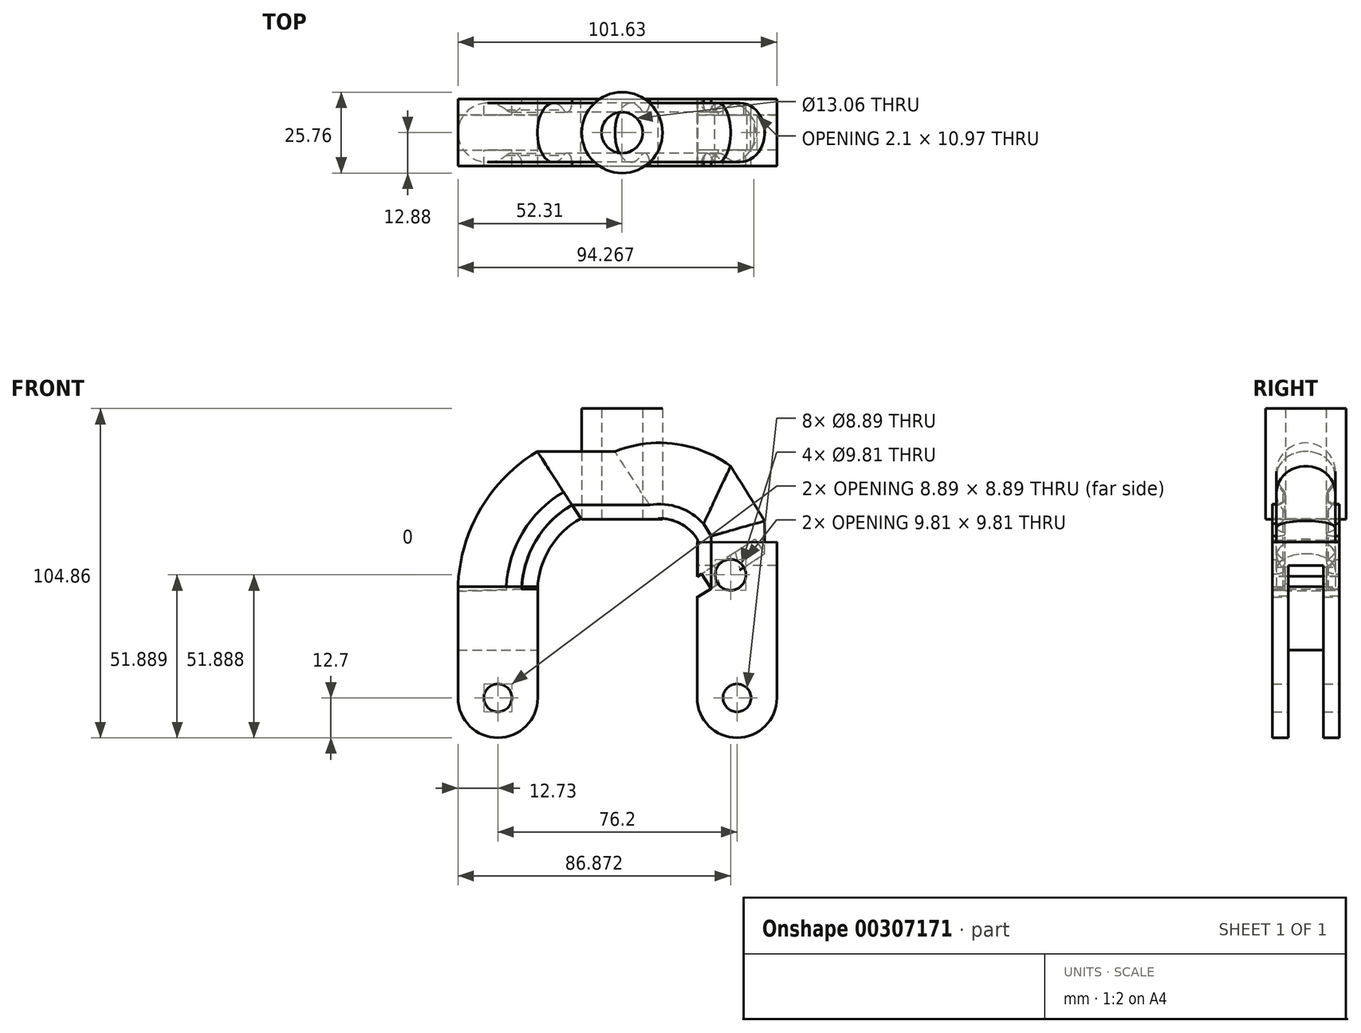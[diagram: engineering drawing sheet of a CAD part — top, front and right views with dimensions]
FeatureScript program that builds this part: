
annotation { "Feature Type Name" : "Feature", "Feature Type Description" : "" }
export const myFeature = defineFeature(function(context is Context, id is Id, definition is map)
    precondition{}
    {
        {
            var Q0;
            Q0=qCreatedBy(makeId("Front.planeOp"),FACE);
            var sketch = newSketch(context, id + "F0", { "sketchPlane" : qUnion([Q0])});
            skCircle(sketch, "E0", {"center": v(-39.58, 0) * mm, "radius": 12.7 * mm});
            skCircle(sketch, "E1", {"center": v(36.62, 0) * mm, "radius": 12.7 * mm});
            skLineSegment(sketch, "E2", {"start": v(-39.58, 0) * mm, "end": v(36.62, 0) * mm, "construction": true});
            skLineSegment(sketch, "E3", {"start": v(23.92, 0) * mm, "end": v(23.92, 49.53) * mm});
            skLineSegment(sketch, "E4", {"start": v(49.32, 0) * mm, "end": v(49.32, 49.66) * mm});
            skCircle(sketch, "E5", {"center": v(34.56, 39.19) * mm, "radius": 4.9 * mm});
            skCircle(sketch, "E6", {"center": v(-39.58, 0) * mm, "radius": 4.45 * mm});
            skCircle(sketch, "E7", {"center": v(36.62, 0) * mm, "radius": 4.45 * mm});
            skLineSegment(sketch, "E8", {"start": v(-26.88, 0) * mm, "end": v(-26.88, 48.71) * mm});
            skLineSegment(sketch, "E9", {"start": v(-26.88, 48.71) * mm, "end": v(-26.88, 0) * mm});
            skLineSegment(sketch, "E10", {"start": v(-52.28, 0) * mm, "end": v(-52.28, 35.38) * mm});
            skLineSegment(sketch, "E11", {"start": v(-52.28, 35.38) * mm, "end": v(-26.88, 35.38) * mm});
            skLineSegment(sketch, "E12", {"start": v(0, 0) * mm, "end": v(0, 75.66) * mm, "construction": true});
            skLineSegment(sketch, "E13", {"start": v(0, 75.66) * mm, "end": v(0, 0) * mm, "construction": true});
            skLineSegment(sketch, "E14", {"start": v(6.53, 56.88) * mm, "end": v(6.53, 92.16) * mm});
            skLineSegment(sketch, "E15", {"start": v(6.53, 92.16) * mm, "end": v(12.88, 92.16) * mm});
            skLineSegment(sketch, "E16", {"start": v(12.88, 92.16) * mm, "end": v(12.88, 56.88) * mm});
            skLineSegment(sketch, "E17", {"start": v(12.88, 56.88) * mm, "end": v(6.53, 56.88) * mm});
            skLineSegment(sketch, "E18", {"start": v(23.92, 49.53) * mm, "end": v(49.32, 49.66) * mm});
            skSolve(sketch);
        }
        {
            var Q0;
            Q0=makeQuery(id+"F0.imprint","IMPRINT",FACE,{"disambiguationData":[TD([[makeQuery(id+"F0.imprint","IMPRINT",EDGE,{"derivedFrom":sQuery(id+"F0.wireOp",EDGE,"E14")}),-1.0]])]});
            var Q1;
            Q1=sQuery(id+"F0.wireOp",EDGE,"E12");
            revolve(context, id + "F1", {"entities" : qUnion([Q0]), "axis" : qUnion([Q1]), "revolveType" : RevolveType.FULL});
        }
        {
            var Q0;
            {var subQ3=sQuery(id+"F0.wireOp",EDGE,"E10");Q0=makeQuery(id+"F0.imprint","IMPRINT",FACE,{"disambiguationData":[TD([[makeQuery(id+"F0.imprint","IMPRINT",EDGE,{"derivedFrom":subQ3}),-1.0]])]});}
            var Q1;
            Q1=makeQuery(id+"F0.imprint","IMPRINT",FACE,{"disambiguationData":[TD([[makeQuery(id+"F0.imprint","IMPRINT",EDGE,{"derivedFrom":sQuery(id+"F0.wireOp",EDGE,"E6")}),-1.0]])]});
            var Q2;
            {var subQ1=sQuery(id+"F0.wireOp",EDGE,"E3");Q2=makeQuery(id+"F0.imprint","IMPRINT",FACE,{"disambiguationData":[TD([[makeQuery(id+"F0.imprint","IMPRINT",EDGE,{"derivedFrom":subQ1}),-1.0]])]});}
            var Q3;
            Q3=makeQuery(id+"F0.imprint","IMPRINT",FACE,{"disambiguationData":[TD([[makeQuery(id+"F0.imprint","IMPRINT",EDGE,{"derivedFrom":sQuery(id+"F0.wireOp",EDGE,"E7")}),-1.0]])]});
            extrude(context, id + "F2", {"entities" : qUnion([Q0, Q1, Q2, Q3]), "endBound" : BoundingType.SYMMETRIC, "depth" : 21.34 * mm});
        }
        {
            var Q0;
            {var subQ1=sQuery(id+"F0.wireOp",EDGE,"E3");Q0=makeQuery(id+"F0.imprint","IMPRINT",FACE,{"disambiguationData":[TD([[makeQuery(id+"F0.imprint","IMPRINT",EDGE,{"derivedFrom":subQ1}),-1.0]])]});}
            var Q1;
            Q1=makeQuery(id+"F0.imprint","IMPRINT",FACE,{"disambiguationData":[TD([[makeQuery(id+"F0.imprint","IMPRINT",EDGE,{"derivedFrom":sQuery(id+"F0.wireOp",EDGE,"E7")}),-1.0]])]});
            var Q2;
            {var subQ3=sQuery(id+"F0.wireOp",EDGE,"E10");Q2=makeQuery(id+"F0.imprint","IMPRINT",FACE,{"disambiguationData":[TD([[makeQuery(id+"F0.imprint","IMPRINT",EDGE,{"derivedFrom":subQ3}),-1.0]])]});}
            var Q3;
            Q3=makeQuery(id+"F0.imprint","IMPRINT",FACE,{"disambiguationData":[TD([[makeQuery(id+"F0.imprint","IMPRINT",EDGE,{"derivedFrom":sQuery(id+"F0.wireOp",EDGE,"E6")}),-1.0]])]});
            extrude(context, id + "F3", {"entities" : qUnion([Q0, Q1, Q2, Q3]), "endBound" : BoundingType.SYMMETRIC, "depth" : 21.34 * mm});
        }
        {
            var Q0;
            Q0=qCreatedBy(makeId("Right.planeOp"),FACE);
            var sketch = newSketch(context, id + "F4", { "sketchPlane" : qUnion([Q0])});
            skPoint(sketch, "E19.middle.positionSnap0", {"position": v(0.3, 18.22) * mm});
            skLineSegment(sketch, "E20", {"start": v(5.59, -32.84) * mm, "end": v(5.59, 42.16) * mm});
            skLineSegment(sketch, "E21", {"start": v(5.59, 42.16) * mm, "end": v(-5.59, 42.16) * mm});
            skLineSegment(sketch, "E22", {"start": v(-5.59, 42.16) * mm, "end": v(-5.59, -33.1) * mm});
            skLineSegment(sketch, "E23", {"start": v(-5.59, -33.1) * mm, "end": v(5.59, -32.84) * mm});
            skLineSegment(sketch, "E24", {"start": v(5.59, 15.24) * mm, "end": v(-5.59, 15.24) * mm});
            skSolve(sketch);
        }
        {
            var Q0;
            {var subQ0=sQuery(id+"F4.wireOp",EDGE,"E23");Q0=makeQuery(id+"F4.imprint","IMPRINT",FACE,{"disambiguationData":[TD([[makeQuery(id+"F4.imprint","IMPRINT",EDGE,{"derivedFrom":subQ0}),1.0]])]});}
            extrude(context, id + "F5", {"entities" : qUnion([Q0]), "operationType" : NewBodyOperationType.REMOVE, "endBound" : BoundingType.THROUGH_ALL, "oppositeDirection" : true, "depth" : 176.53 * mm});
        }
        {
            var Q0;
            {var subQ0=sQuery(id+"F4.wireOp",EDGE,"E23");Q0=makeQuery(id+"F4.imprint","IMPRINT",FACE,{"disambiguationData":[TD([[makeQuery(id+"F4.imprint","IMPRINT",EDGE,{"derivedFrom":subQ0}),1.0]])]});}
            var Q1;
            {var subQ0=sQuery(id+"F4.wireOp",EDGE,"E21");Q1=makeQuery(id+"F4.imprint","IMPRINT",FACE,{"disambiguationData":[TD([[makeQuery(id+"F4.imprint","IMPRINT",EDGE,{"derivedFrom":subQ0}),1.0]])]});}
            extrude(context, id + "F6", {"entities" : qUnion([Q0, Q1]), "operationType" : NewBodyOperationType.REMOVE, "endBound" : BoundingType.THROUGH_ALL, "depth" : 25.4 * mm});
        }
        {
            var Q0;
            Q0=makeQuery(id+"F2.opExtrude","SWEPT_FACE",FACE,{"disambiguationData":[OSD([sQuery(id+"F0.wireOp",EDGE,"E11")])]});
            var sketch = newSketch(context, id + "F7", { "sketchPlane" : qUnion([Q0])});
            skArc(sketch, "E25", {"start": v(-36.33, 6.74) * mm, "mid": v(-51.88, 2.71) * mm, "end": v(-41.14, -9.24) * mm});
            skLineSegment(sketch, "E26.bottom", {"start": v(-26.88, -10.67) * mm, "end": v(-36.33, -10.67) * mm});
            skLineSegment(sketch, "E26.top", {"start": v(-26.88, 10.67) * mm, "end": v(-36.33, 10.67) * mm});
            skLineSegment(sketch, "E26.left", {"start": v(-26.88, -10.67) * mm, "end": v(-26.88, 10.67) * mm});
            skArc(sketch, "E27", {"start": v(-49.72, -6.45) * mm, "mid": v(-43.47, -9.38) * mm, "end": v(-36.9, -7.25) * mm});
            skLineSegment(sketch, "E28", {"start": v(-31.96, -10.67) * mm, "end": v(-31.96, -9.57) * mm});
            skLineSegment(sketch, "E29", {"start": v(-31.96, 10.67) * mm, "end": v(-26.88, 10.67) * mm});
            skLineSegment(sketch, "E30", {"start": v(-31.96, -10.67) * mm, "end": v(-26.88, -10.67) * mm});
            skArc(sketch, "E31", {"start": v(-36.9, 7.25) * mm, "mid": v(-33.7, 6.84) * mm, "end": v(-31.96, 9.57) * mm});
            skArc(sketch, "E32.MirrorCS", {"start": v(-36.9, -7.25) * mm, "mid": v(-33.7, -6.84) * mm, "end": v(-31.96, -9.57) * mm});
            skArc(sketch, "E33.trimOffspring", {"start": v(-36.33, 6.74) * mm, "mid": v(-46.54, 8.66) * mm, "end": v(-52.28, 0) * mm});
            skLineSegment(sketch, "E34.trimOffspring", {"start": v(-31.96, 9.57) * mm, "end": v(-31.96, 10.67) * mm});
            skSolve(sketch);
        }
        {
            var Q0;
            Q0=qCreatedBy(makeId("Front.planeOp"),FACE);
            var sketch = newSketch(context, id + "F8", { "sketchPlane" : qUnion([Q0])});
            skLineSegment(sketch, "E35", {"start": v(-12.77, 56.5) * mm, "end": v(11.98, 56.5) * mm});
            skArc(sketch, "E36", {"start": v(-12.77, 56.5) * mm, "mid": v(-22.3, 47.34) * mm, "end": v(-26.12, 34.7) * mm});
            skArc(sketch, "E37", {"start": v(23.46, 50.11) * mm, "mid": v(18.55, 54.8) * mm, "end": v(11.98, 56.5) * mm});
            skLineSegment(sketch, "E38", {"start": v(23.46, 50.11) * mm, "end": v(23.46, 31.63) * mm});
            skSolve(sketch);
        }
        {
            var Q0;
            {var subQ3=sQuery(id+"F7.wireOp",EDGE,"E25");Q0=makeQuery(id+"F7.imprint","IMPRINT",FACE,{"disambiguationData":[TD([[makeQuery(id+"F7.imprint","IMPRINT",EDGE,{"derivedFrom":subQ3}),1.0]])]});}
            var Q1;
            Q1=sQuery(id+"F8.wireOp",EDGE,"E36");
            sweep(context, id + "F9", {"profiles" : qUnion([Q0]), "path" : qUnion([Q1])});
        }
        {
            var Q0;
            Q0=makeQuery(id+"F9.opSweep","CAP_FACE",FACE,{"disambiguationData":[OSD([sQuery(id+"F7.wireOp",EDGE,"E25"),sQuery(id+"F7.wireOp",EDGE,"E27"),sQuery(id+"F7.wireOp",EDGE,"E28"),sQuery(id+"F7.wireOp",EDGE,"E29"),sQuery(id+"F7.wireOp",EDGE,"E30"),sQuery(id+"F7.wireOp",EDGE,"E26.left"),sQuery(id+"F7.wireOp",EDGE,"E31"),sQuery(id+"F7.wireOp",EDGE,"E32.MirrorCS"),sQuery(id+"F7.wireOp",EDGE,"E33.trimOffspring"),sQuery(id+"F7.wireOp",EDGE,"E34.trimOffspring"),sQuery(id+"F8.wireOp",VERTEX,"E36.start")])],"isStart":false});
            var Q1;
            Q1=sQuery(id+"F8.wireOp",EDGE,"E35");
            var Q2;
            Q2=sQuery(id+"F8.wireOp",EDGE,"E37");
            var Q3;
            Q3=sQuery(id+"F8.wireOp",EDGE,"E38");
            sweep(context, id + "F10", {"profiles" : qUnion([Q0]), "path" : qUnion([Q1, Q2, Q3])});
        }
        {
            var Q0;
            Q0=makeQuery(id+"F10.opSweep","CAP_FACE",FACE,{"disambiguationData":[OSD([sQuery(id+"F7.wireOp",EDGE,"E25"),sQuery(id+"F7.wireOp",EDGE,"E27"),sQuery(id+"F7.wireOp",EDGE,"E28"),sQuery(id+"F7.wireOp",EDGE,"E29"),sQuery(id+"F7.wireOp",EDGE,"E30"),sQuery(id+"F7.wireOp",EDGE,"E26.left"),sQuery(id+"F7.wireOp",EDGE,"E31"),sQuery(id+"F7.wireOp",EDGE,"E32.MirrorCS"),sQuery(id+"F7.wireOp",EDGE,"E33.trimOffspring"),sQuery(id+"F7.wireOp",EDGE,"E34.trimOffspring"),sQuery(id+"F8.wireOp",VERTEX,"E36.start"),sQuery(id+"F8.wireOp",VERTEX,"E38.end")])],"isStart":false});
            extrude(context, id + "F11", {"entities" : qUnion([Q0]), "operationType" : NewBodyOperationType.REMOVE, "oppositeDirection" : true, "depth" : 5.6 * mm});
        }
    });
